# Revit family: WHS
name_source: partatom
category: Pipe Accessories
units: mm (PartAtom-declared; Revit-internal decimal feet)

## family parameters
Always vertical = Yes
Classification Number = 23.60.30.11.14.11
Cut with Voids When Loaded = No
Part Type = Normal
Round Connector Dimension = Use Diameter
Shared = No
Work Plane-Based = No

## types (9) — shared parameters
Default Elevation = 0' - 0"
Description = Water Hammer Arrestors For Heavy Equipment
Manufacturer = Mifab
Model = WHS
URL = www.mifab.com

## per-type parameters (varying)
| type | Diameter | Height | Material | NPSM Size |
| WHS-11 | 0' - 10 1/2" | 0' - 8" | Carbon Steel | 0' - 2" |
| WHS-12 | 0' - 10 1/2" | 0' - 10" | Metal-Watts-Copper | 0' - 2" |
| WHS-13 | 1' - 4" | 0' - 10 3/4" | Metal-Watts-Copper | 0' - 2" |
| WHS-14 | 1' - 4" | 1' - 2" | Metal-Watts-Copper | 0' - 2" |
| WHS-15 | 2' - 0" | 1' - 6" | Metal-Watts-Copper | 0' - 3" |
| WHS-16 | 2' - 0" | 1' - 10 3/4" | Metal-Watts-Copper | 0' - 3" |
| WHS-17 | 3' - 0" | 2' - 1" | Metal-Watts-Copper | 0' - 4" |
| WHS-17S | 3' - 6" | 3' - 4" | Metal-Watts-Copper | 0' - 6" |
| WHS-18 | 4' - 0" | 3' - 11" | Metal-Watts-Copper | 0' - 6" |

## geometry (parser evidence)
native form markers: Blend x6, Sweep x2
no freeform markers — native parametric forms only
